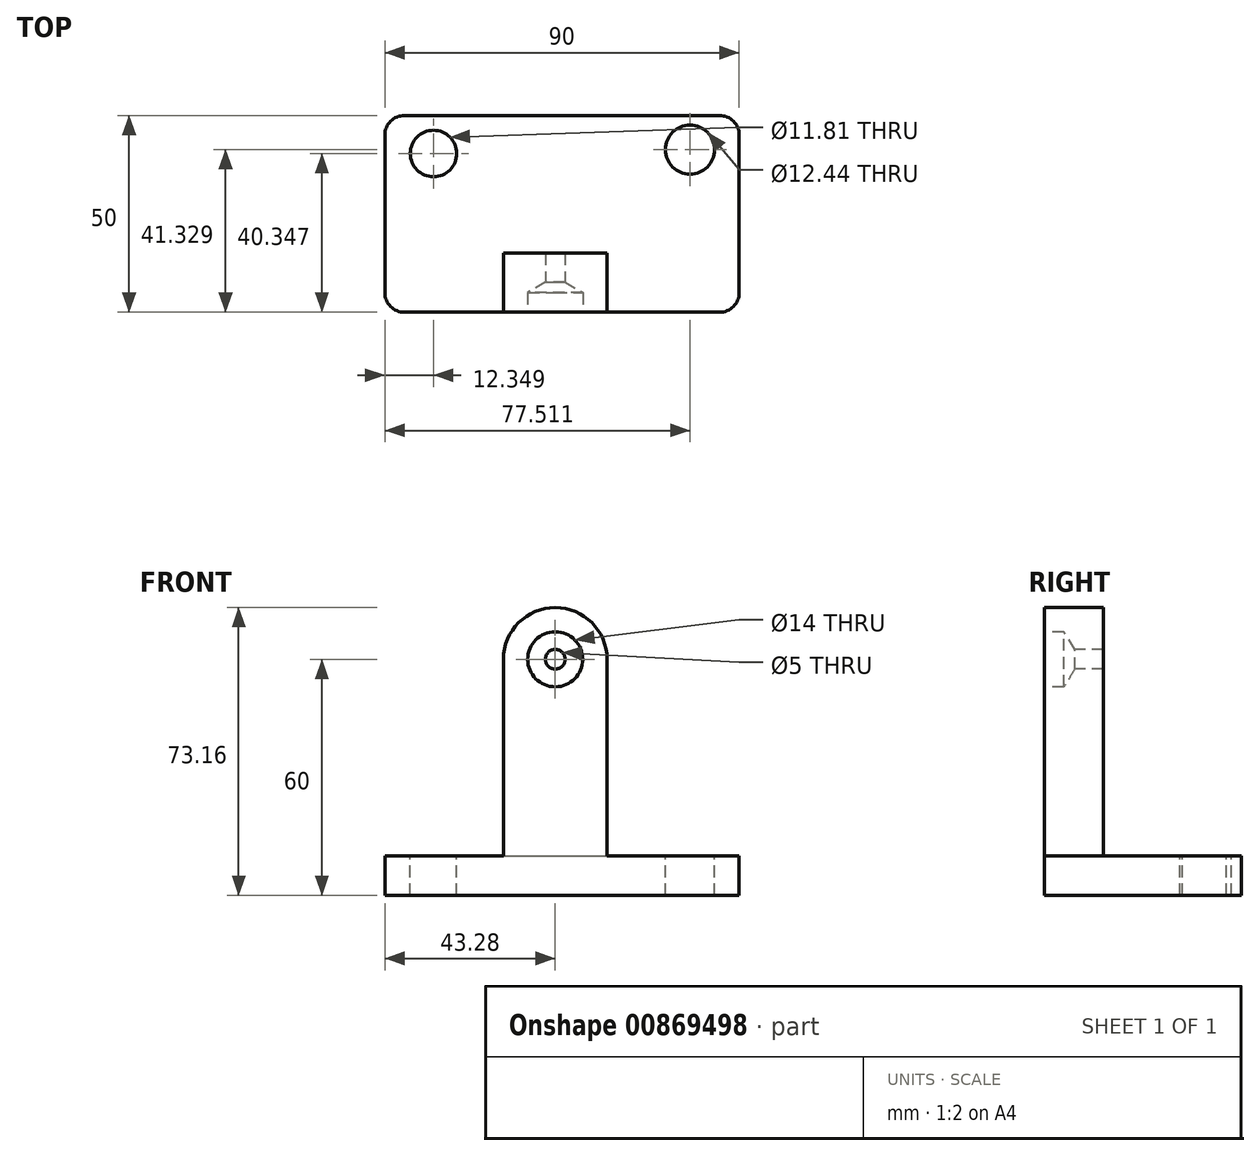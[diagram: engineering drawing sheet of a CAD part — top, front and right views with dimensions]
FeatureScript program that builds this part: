
annotation { "Feature Type Name" : "Feature", "Feature Type Description" : "" }
export const myFeature = defineFeature(function(context is Context, id is Id, definition is map)
    precondition{}
    {
        {
            var Q0;
            Q0=qCreatedBy(makeId("Top.planeOp"),FACE);
            var sketch = newSketch(context, id + "F0", { "sketchPlane" : qUnion([Q0])});
            skLineSegment(sketch, "E0.bottom", {"start": v(-43.28, 50) * mm, "end": v(46.72, 50) * mm});
            skLineSegment(sketch, "E0.top", {"start": v(-43.28, 0) * mm, "end": v(46.72, 0) * mm});
            skLineSegment(sketch, "E0.left", {"start": v(-43.28, 50) * mm, "end": v(-43.28, 0) * mm});
            skLineSegment(sketch, "E0.right", {"start": v(46.72, 50) * mm, "end": v(46.72, 0) * mm});
            skCircle(sketch, "E1", {"center": v(-30.93, 40.35) * mm, "radius": 5.9 * mm});
            skCircle(sketch, "E2", {"center": v(34.23, 41.33) * mm, "radius": 6.22 * mm});
            skSolve(sketch);
        }
        {
            var Q0;
            Q0=qCreatedBy(makeId("Front.planeOp"),FACE);
            var sketch = newSketch(context, id + "F1", { "sketchPlane" : qUnion([Q0])});
            skLineSegment(sketch, "E3", {"start": v(13.16, 0) * mm, "end": v(13.16, 50) * mm});
            skLineSegment(sketch, "E4", {"start": v(-13.16, 50) * mm, "end": v(-13.16, 0) * mm});
            skLineSegment(sketch, "E5", {"start": v(-13.16, 0) * mm, "end": v(13.16, 0) * mm});
            skLineSegment(sketch, "E6", {"start": v(-13.16, 50) * mm, "end": v(13.16, 50) * mm});
            skArc(sketch, "E7", {"start": v(-13.16, 50) * mm, "mid": v(0, 63.16) * mm, "end": v(13.16, 50) * mm});
            skSolve(sketch);
        }
        {
            var Q0;
            Q0=makeQuery(id+"F0.imprint","IMPRINT",FACE,{"disambiguationData":[TD([[makeQuery(id+"F0.imprint","IMPRINT",EDGE,{"derivedFrom":sQuery(id+"F0.wireOp",EDGE,"E0.bottom")}),-1.0]])]});
            extrude(context, id + "F2", {"entities" : qUnion([Q0]), "oppositeDirection" : true, "depth" : 10 * mm, "offsetDistance" : 25 * mm});
        }
        {
            var Q0;
            Q0 = qSketchRegion(id + "F1", true);
            extrude(context, id + "F3", {"entities" : qUnion([Q0]), "operationType" : NewBodyOperationType.ADD, "oppositeDirection" : true, "depth" : 15 * mm, "offsetDistance" : 25 * mm});
        }
        {
            var Q0;
            Q0=makeQuery(id+"F2.opExtrude","SWEPT_EDGE",EDGE,{"disambiguationData":[OSD([sQuery(id+"F0.wireOp",EDGE,"E0.top"),sQuery(id+"F0.wireOp",EDGE,"E0.right")])]});
            var Q1;
            Q1=makeQuery(id+"F2.opExtrude","SWEPT_EDGE",EDGE,{"disambiguationData":[OSD([sQuery(id+"F0.wireOp",EDGE,"E0.bottom"),sQuery(id+"F0.wireOp",EDGE,"E0.right")])]});
            var Q2;
            Q2=makeQuery(id+"F2.opExtrude","SWEPT_EDGE",EDGE,{"disambiguationData":[OSD([sQuery(id+"F0.wireOp",EDGE,"E0.bottom"),sQuery(id+"F0.wireOp",EDGE,"E0.left")])]});
            var Q3;
            Q3=makeQuery(id+"F2.opExtrude","SWEPT_EDGE",EDGE,{"disambiguationData":[OSD([sQuery(id+"F0.wireOp",EDGE,"E0.top"),sQuery(id+"F0.wireOp",EDGE,"E0.left")])]});
            fillet(context, id + "F4", {"entities" : qUnion([Q0, Q1, Q2, Q3]), "radius" : 5 * mm, "tangentPropagation" : true, "allowEdgeOverflow" : false});
        }
        {
            var Q0;
            Q0=sQuery(id+"F1.wireOp",VERTEX,"E7.center");
            var Q1;
            Q1=makeQuery(id+"F2.opExtrude","SWEPT_BODY",BODY,{"disambiguationData":[OSD([sQuery(id+"F0.wireOp",EDGE,"E0.bottom"),sQuery(id+"F0.wireOp",EDGE,"E0.top"),sQuery(id+"F0.wireOp",EDGE,"E0.left"),sQuery(id+"F0.wireOp",EDGE,"E0.right"),sQuery(id+"F0.wireOp",EDGE,"E1"),sQuery(id+"F0.wireOp",EDGE,"E2")])]});
            hole(context, id + "F5", {"style" : HoleStyle.SIMPLE, "endStyle" : HoleEndStyle.BLIND, "holeDiameter" : 14 * mm, "majorDiameter" : 5 * mm, "holeDepth" : 5 * mm, "isTappedThrough" : true, "tappedDepth" : 12 * mm, "tapClearance" : 3, "locations" : qUnion([Q0]), "scope" : qUnion([Q1])});
        }
        {
            var Q0;
            Q0=sQuery(id+"F1.wireOp",VERTEX,"E7.center");
            var Q1;
            Q1=makeQuery(id+"F2.opExtrude","SWEPT_BODY",BODY,{"disambiguationData":[OSD([sQuery(id+"F0.wireOp",EDGE,"E0.bottom"),sQuery(id+"F0.wireOp",EDGE,"E0.top"),sQuery(id+"F0.wireOp",EDGE,"E0.left"),sQuery(id+"F0.wireOp",EDGE,"E0.right"),sQuery(id+"F0.wireOp",EDGE,"E1"),sQuery(id+"F0.wireOp",EDGE,"E2")])]});
            hole(context, id + "F6", {"style" : HoleStyle.SIMPLE, "endStyle" : HoleEndStyle.THROUGH, "holeDiameter" : 5 * mm, "majorDiameter" : 5 * mm, "isTappedThrough" : true, "tappedDepth" : 12 * mm, "tapClearance" : 3, "locations" : qUnion([Q0]), "scope" : qUnion([Q1])});
        }
    });
